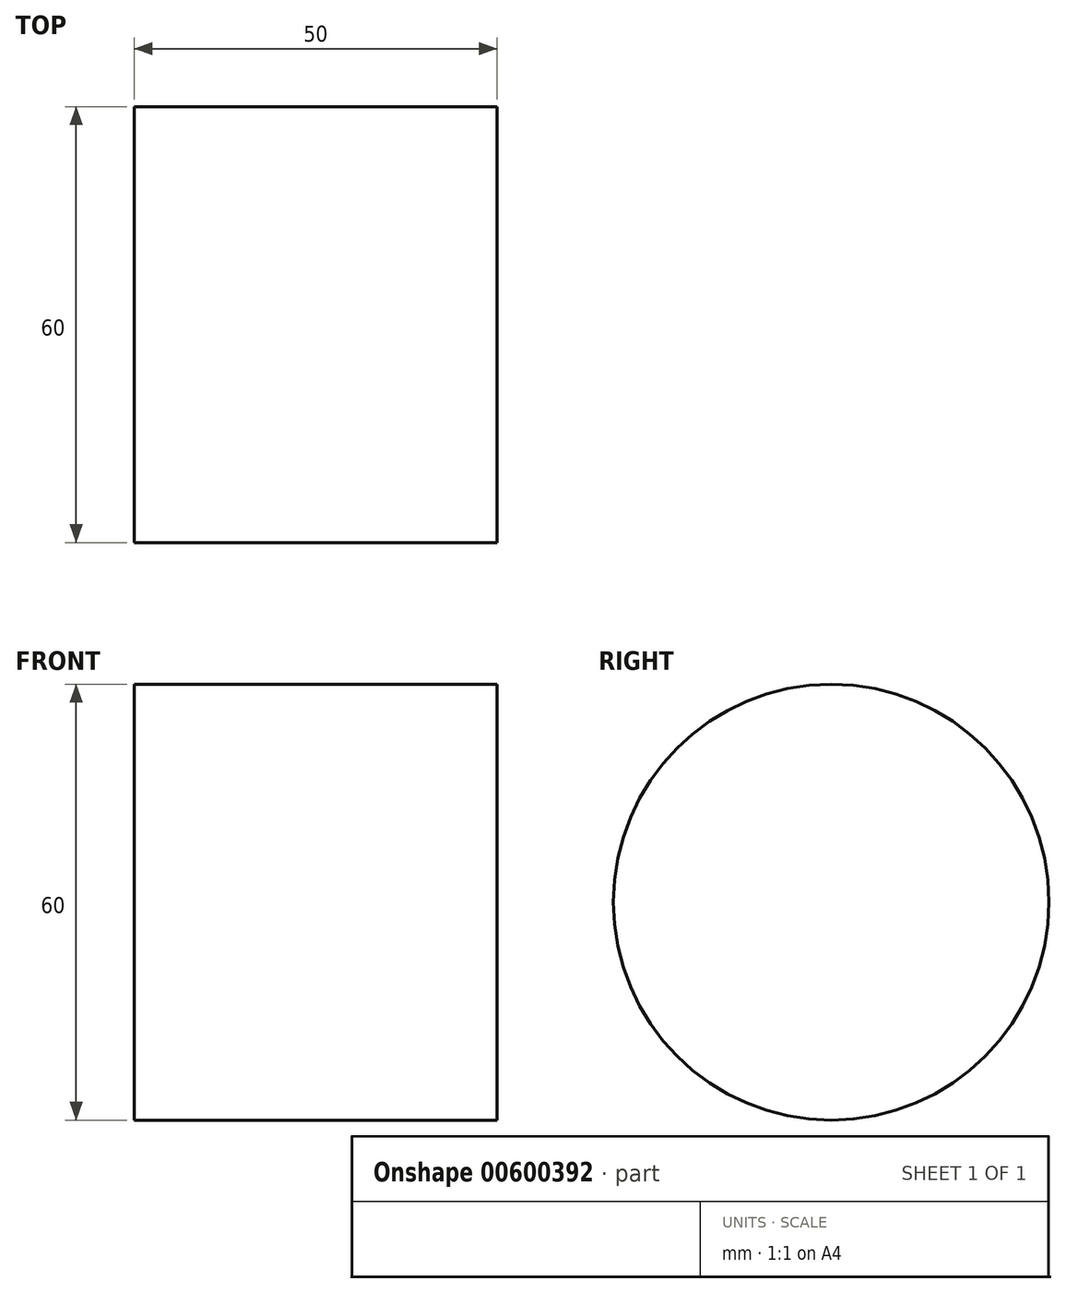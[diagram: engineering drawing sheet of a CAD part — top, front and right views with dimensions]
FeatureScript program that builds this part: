
annotation { "Feature Type Name" : "Feature", "Feature Type Description" : "" }
export const myFeature = defineFeature(function(context is Context, id is Id, definition is map)
    precondition{}
    {
        {
            var Q0;
            Q0=qCreatedBy(makeId("Front.planeOp"),FACE);
            var sketch = newSketch(context, id + "F0", { "sketchPlane" : qUnion([Q0])});
            skLineSegment(sketch, "E0", {"start": v(0, 0) * mm, "end": v(0, 30) * mm});
            skLineSegment(sketch, "E1", {"start": v(0, 30) * mm, "end": v(50, 30) * mm});
            skLineSegment(sketch, "E2", {"start": v(50, 30) * mm, "end": v(50, 0) * mm});
            skLineSegment(sketch, "E3", {"start": v(50, 0) * mm, "end": v(0, 0) * mm});
            skSolve(sketch);
        }
        {
            var Q0;
            Q0=makeQuery(id+"F0.imprint","IMPRINT",FACE,{"disambiguationData":[TD([[makeQuery(id+"F0.imprint","IMPRINT",EDGE,{"derivedFrom":sQuery(id+"F0.wireOp",EDGE,"E0")}),-1.0]])]});
            var Q1;
            Q1=sQuery(id+"F0.wireOp",EDGE,"E3");
            revolve(context, id + "F1", {"entities" : qUnion([Q0]), "axis" : qUnion([Q1]), "revolveType" : RevolveType.FULL});
        }
    });
